# Revit family: Drain_Thoroflush_Zurn-Z300
name_source: partatom
category: Plumbing Fixtures
units: mm (PartAtom-declared; Revit-internal decimal feet)

## family parameters
Always vertical = Yes
Cut with Voids When Loaded = No
Maintain Annotation Orientation = No
OmniClass Number = 23.45.55.21
OmniClass Title = Drains (Wastes)
Part Type = Normal
Room Calculation Point = No
Round Connector Dimension = Use Radius
Shared = No
Work Plane-Based = No

## types (6) — shared parameters
Approx. Weight (Lbs) = 50 "
Assembly Code = D2030300
CW Connection = No
Default Elevation = 25 "
Description = THOROFLUSH DRAIN
Grate Open Area Sq.in = 18 "
HW Connection = No
Main Material = Cast Iron - Zurn - White A.R.E Coated - Interior
Manufacturer = Zurn Water, LLC
Manufacurer Brand = Zurn
Modified Date = 11/26/2025
Outlet Trap Radius  (Inner) = 0.412 "
Outlet Trap Radius  (Nominal) = 0.375 "
Outlet Trap Radius (Actual) = 0.525 "
Product Documentation Link = https://files.zurn.com
Product Installation Sheet = https://files.zurn.com
Product Page URL = https://www.zurn.com
Product data url = https://www.bimobject.com
Thoroflush Drain = 11 "
Trap Connection Radius (Actual) = 0.42 "
Trap Connection Radius (Inner) = 0.311 "
Trap Connection Radius (Nominal) = 0.25 "
URL = www.zurn.com
Vent Connection = No
WFU = 1
Waste Connection = Yes
zero-valued in all types: CWFU, HWFU

## per-type parameters (varying)
| type | A_ Pipe Size (Actual-Inner) | A_ Pipe Size (Actual-Outer) | A_ Pipe Size (Nominal) | Body Height | Connector Radius | Dimension m | Distance to Pipe Face | Frame and Grate | Model | Pipe to Pipe Distance | Trap Depth | Width |
| ZB300-2 Inch Threaded Outlet | 1.034 " | 1.188 " | 2 " | 9.25 " | 1 " | 3 " | 7.25 " | Bronze - Zurn - Polished | ZB300 | 4.5 " | 3.375 " | 14.5 " |
| ZB300-3 Inch Threaded Outlet | 1.534 " | 1.75 " | 3 " | 9.25 " | 1.5 " | 2.5 " | 7.25 " | Bronze - Zurn - Polished | ZB300 | 4.5 " | 3.875 " | 14.5 " |
| ZB300-4 Inch Threaded Outlet | 2.013 " | 2.25 " | 4 " | 11.75 " | 2 " | 3 " | 8.25 " | Bronze - Zurn - Polished | ZB300 | 5 " | 4.688 " | 15.5 " |
| ZN300-2 Inch Threaded Outlet | 1.034 " | 1.188 " | 2 " | 9.25 " | 1 " | 3 " | 7.25 " | Bronze - Zurn - Polished Nickel | ZN300 | 4.5 " | 3.375 " | 14.5 " |
| ZN300-3 Inch Threaded Outlet | 1.534 " | 1.75 " | 3 " | 9.25 " | 1.5 " | 2.5 " | 7.25 " | Bronze - Zurn - Polished Nickel | ZN300 | 4.5 " | 3.875 " | 14.5 " |
| ZN300-4 Inch Threaded Outlet | 2.013 " | 2.25 " | 4 " | 11.75 " | 2 " | 3 " | 8.25 " | Bronze - Zurn - Polished Nickel | ZN300 | 5 " | 4.688 " | 15.5 " |

## geometry (parser evidence)
native form markers: Sweep x3
no freeform markers — native parametric forms only
